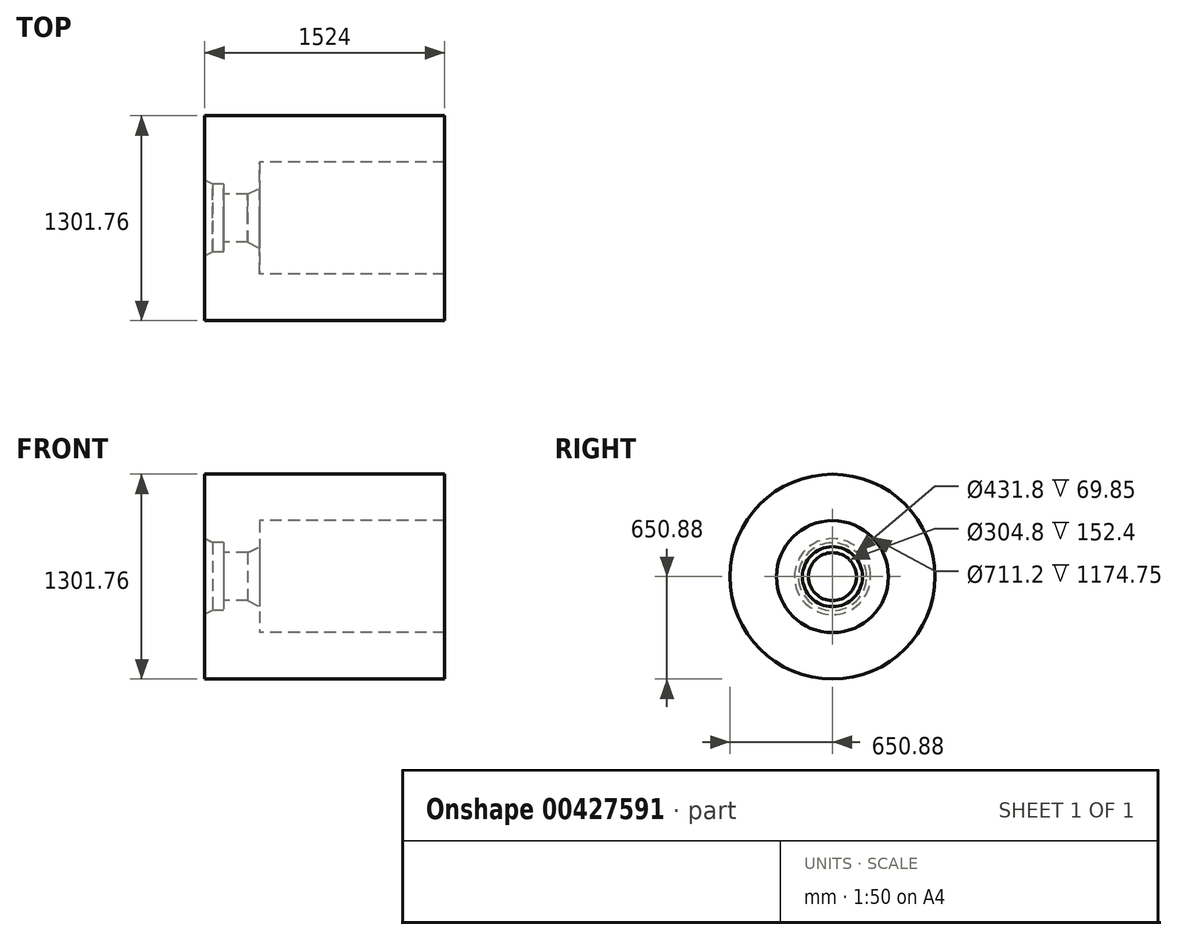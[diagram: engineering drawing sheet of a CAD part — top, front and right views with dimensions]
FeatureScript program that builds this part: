
annotation { "Feature Type Name" : "Feature", "Feature Type Description" : "" }
export const myFeature = defineFeature(function(context is Context, id is Id, definition is map)
    precondition{}
    {
        {
            var Q0;
            Q0=qCreatedBy(makeId("Front.planeOp"),FACE);
            var sketch = newSketch(context, id + "F0", { "sketchPlane" : qUnion([Q0])});
            skLineSegment(sketch, "E0", {"start": v(-648.56, 0) * mm, "end": v(875.44, 0) * mm, "construction": true});
            skLineSegment(sketch, "E1", {"start": v(-648.56, 469.9) * mm, "end": v(875.44, 469.9) * mm});
            skLineSegment(sketch, "E2", {"start": v(875.44, 469.9) * mm, "end": v(875.44, 355.6) * mm});
            skLineSegment(sketch, "E3", {"start": v(875.44, 355.6) * mm, "end": v(-299.3, 355.6) * mm});
            skLineSegment(sketch, "E4", {"start": v(-299.3, 355.6) * mm, "end": v(-299.3, 190.5) * mm});
            skLineSegment(sketch, "E5", {"start": v(-299.3, 190.5) * mm, "end": v(-375.5, 152.4) * mm});
            skLineSegment(sketch, "E6", {"start": v(-375.5, 152.4) * mm, "end": v(-527.9, 152.4) * mm});
            skLineSegment(sketch, "E7", {"start": v(-527.9, 152.4) * mm, "end": v(-527.9, 215.9) * mm});
            skLineSegment(sketch, "E8", {"start": v(-527.9, 215.9) * mm, "end": v(-597.76, 215.9) * mm});
            skLineSegment(sketch, "E9", {"start": v(-597.76, 215.9) * mm, "end": v(-648.56, 241.3) * mm});
            skLineSegment(sketch, "E10", {"start": v(-648.56, 241.3) * mm, "end": v(-648.56, 469.9) * mm});
            skLineSegment(sketch, "E11", {"start": v(875.44, 469.9) * mm, "end": v(875.44, 650.88) * mm});
            skLineSegment(sketch, "E12", {"start": v(875.44, 650.88) * mm, "end": v(-648.56, 650.88) * mm});
            skLineSegment(sketch, "E13", {"start": v(-648.56, 650.88) * mm, "end": v(-648.56, 469.9) * mm});
            skSolve(sketch);
        }
        {
            var Q0;
            Q0=makeQuery(id+"F0.imprint","IMPRINT",FACE,{"disambiguationData":[TD([[makeQuery(id+"F0.imprint","IMPRINT",EDGE,{"derivedFrom":sQuery(id+"F0.wireOp",EDGE,"E1")}),-1.0]])]});
            var Q1;
            Q1=makeQuery(id+"F0.imprint","IMPRINT",FACE,{"disambiguationData":[TD([[makeQuery(id+"F0.imprint","IMPRINT",EDGE,{"derivedFrom":sQuery(id+"F0.wireOp",EDGE,"E1")}),1.0]])]});
            var Q2;
            Q2=sQuery(id+"F0.wireOp",EDGE,"E0");
            revolve(context, id + "F1", {"surfaceOperationType" : NewSurfaceOperationType.NEW, "entities" : qUnion([Q0, Q1]), "axis" : qUnion([Q2]), "revolveType" : RevolveType.FULL});
        }
    });
